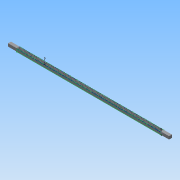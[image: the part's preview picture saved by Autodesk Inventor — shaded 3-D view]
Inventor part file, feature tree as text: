
AUTODESK INVENTOR PART (.ipt)
format: ipt  version: 2015 (Build 190159000, 159)  size: 1,909,248 bytes
history: native  units: in
note: dims shown in document units (in); Inventor stores cm internally (conversion verified against a paired STEP export)
features: sketch x4, projected_geometry x3, other x2, extrude x2, imported_body x1
ambient origin geometry x8: Origin, YZ Plane, XZ Plane, XY Plane, X Axis, Y Axis, Z Axis, Center Point
bodies: Body1 (feature_tree)
feature tree (12):
  parser-record x1  (decoder bookkeeping rows leaked as tree rows — omitted from the tree; the rows remain in map.json)
  other  "KKS10-10-51"
  sketch  "Sketch1"  dims[d2=0.0394in d3=0.0394in]
  sketch  "Sketch2"  dims[d10=19.685in d11=0.5906in]
  extrude  "Extrusion2"  Depth=0.0394in
  extrude  "Extrusion3"  Depth=19.685in
  imported_body  "Base1"
  projected_geometry  "Projected Loop1"
  projected_geometry  "Projected Loop2"
  sketch  "Sketch4"  dims[d12=0.3937in d13=0.0in]
  sketch  "Sketch5"  dims[d14=0.3937in d15=1.1811in d16=0.3937in d17=1.1811in d18=0.3937in d19=0.0in]
  projected_geometry  "Projected Loop4"
